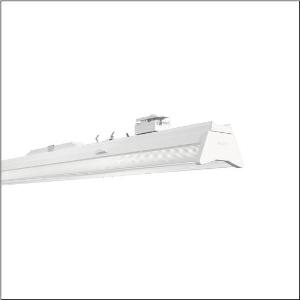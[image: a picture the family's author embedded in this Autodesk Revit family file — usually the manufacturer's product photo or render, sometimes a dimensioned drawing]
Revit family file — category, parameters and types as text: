
# Revit family: licross_r__11_performance_ho_51td16dn6exm_746f
name_source: partatom
category: Lighting Fixtures
units: mm (PartAtom-declared; Revit-internal decimal feet)

## family parameters
Cut with Voids When Loaded = No
Host = Face
Light Source = No
Part Type = Normal
Room Calculation Point = No
Round Connector Dimension = Use Diameter
Shared = No

## types (1)
- --- (1 x LED, 14180 lm, 81.4 W, 6500K)
    Apparent Load = 81 VA
    CIE Flux Codes = 63 87 95 78 100
    Color Rendering = 80
    Color Temperature = 6500K
    Default Elevation = 1800 mm
    Description = Licross® 11 Performance HO, luminaire insert, of sheet steel, galvanised, coil coated, white, length: 1.500mm, width: 120mm, height: 123mm, LED rated luminous flux: 14.180lm, light colour: 865, control gear: DALI 2, with plug, 5-pole, with phase selection, mains connection: 220..240V, AC, 50/60Hz, rated input power: 81W, halogen-free wiring, primary light control with lens, of plastic, primary optical cover: cover, of PMMA, light emission: direct/indirect distribution, primary light characteristic: symmetric, protection rating (complete): IP54, insulation class (complete): insulation class I (protective earthing), certification: CE, ENEC, VDE, UKCA, protection symbol: D if used in an environment with non-conductive dust loads with corresponding accessories, impact resistance: IK06, permissible ambient temperature for indoor applications: -25..+35°C, corresponds to IFS (International Featured Standards) requirements for safety and quality in the food industry, reducing of maximum allowable ambient temperature of 5°C with ceiling mounting, LABS conformity tested according to VDMA 24364:2018-05, packaging unit: 1 piece
    Height = 114 mm
    Lamp = 1 x LED
    Lamp Light Flux = 14180 lm
    Lamp Power = 81.4 W
    Lamp count = 1
    Length = 1500 mm
    Luminous efficacy = 174 lm/W
    Manufacturer = Siteco
    ModVariant = No
    Model = 51TD16DN6EXM
    Mounting Place = Ceiling
    Mounting Type = Pendant
    Number of Poles = 1
    OnlyDefault = Yes
    Power Factor = 1
    Product Name = Licross® 11 Performance HO
    Product group = luminaire insert
    ProductGroupID = 901
    Protection Class = Protection class I
    Protection Degree = IP 54
    RLX_Detail_Level = 1
    RLX_Emergency_Light_Flux = 0 lm
    RLX_Emergency_Type = 0
    RLX_Emergency_Type_DB = No
    RlxData = <blob elided: 34097 chars, md5=5e783577>
    Socket = socket
    Standby Power = 0 W
    System Light Flux = 14180 lm
    System Power = 81 W
    Type Comments = factory setting: luminous flux: 100 % | dim-lin: 254 | 550 mA
    Type Image = l_1256138.jpg
    URL = http://relux.com
    VarID = @adj_036273
    Voltage = 0 V
    Weight = 0.00 kg
    Width = 120 mm

## geometry (parser evidence)
native form markers: Blend x4, Sweep x14
no freeform markers — native parametric forms only
